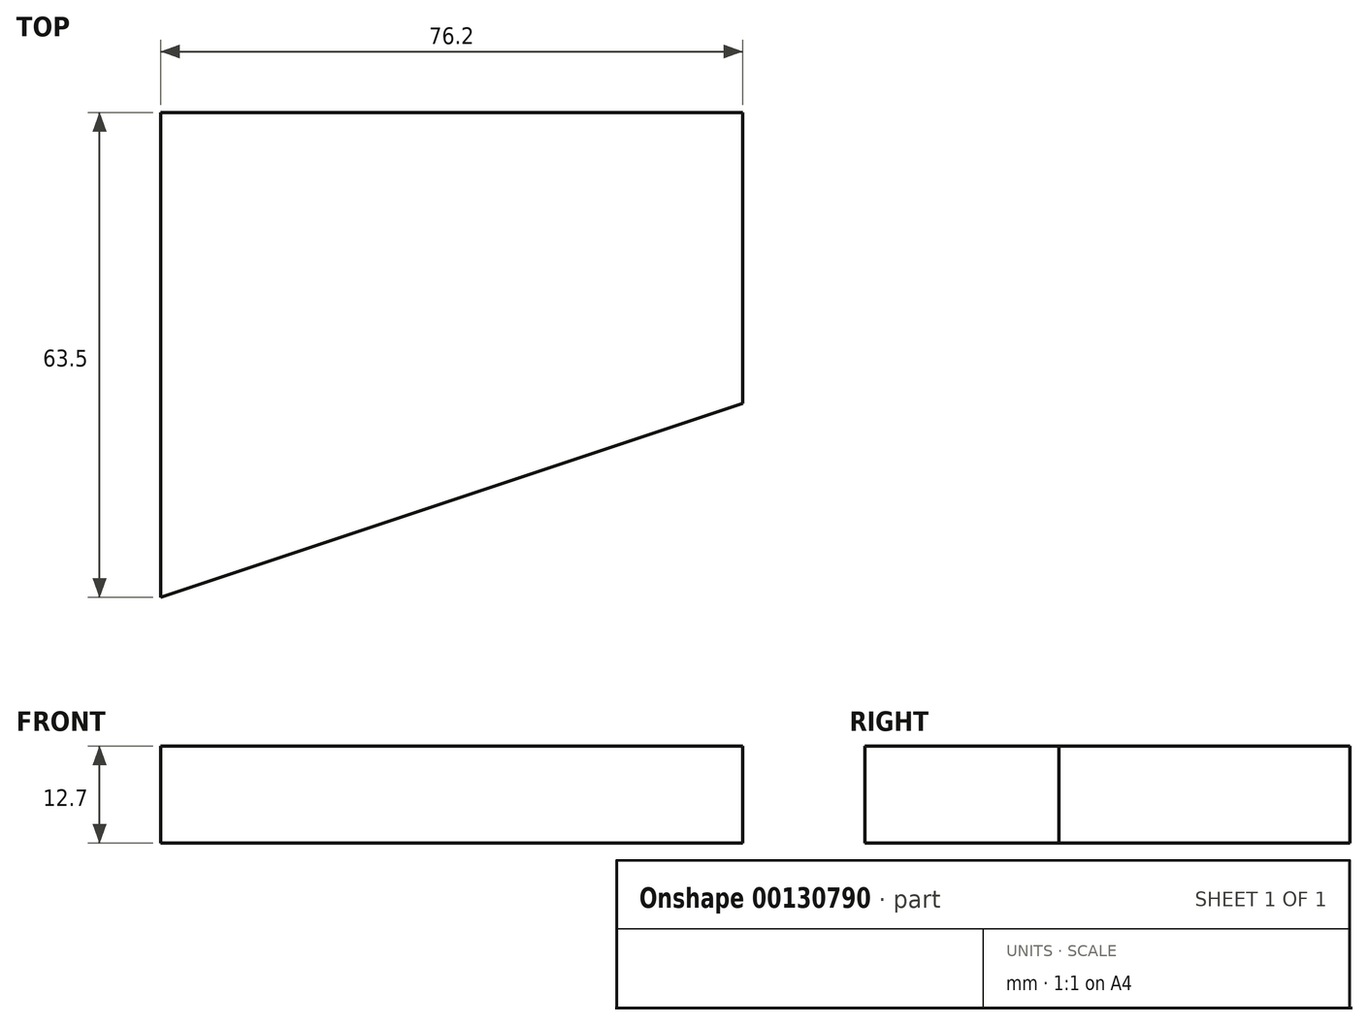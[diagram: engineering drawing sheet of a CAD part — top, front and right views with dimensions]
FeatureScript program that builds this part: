
annotation { "Feature Type Name" : "Feature", "Feature Type Description" : "" }
export const myFeature = defineFeature(function(context is Context, id is Id, definition is map)
    precondition{}
    {
        {
            var Q0;
            Q0=qCreatedBy(makeId("Front.planeOp"),FACE);
            var sketch = newSketch(context, id + "F0", { "sketchPlane" : qUnion([Q0])});
            skLineSegment(sketch, "E0.bottom", {"start": v(0, 0) * mm, "end": v(76.2, 0) * mm});
            skLineSegment(sketch, "E0.top", {"start": v(0, 50.8) * mm, "end": v(76.2, 50.8) * mm});
            skLineSegment(sketch, "E0.left", {"start": v(0, 0) * mm, "end": v(0, 50.8) * mm});
            skLineSegment(sketch, "E0.right", {"start": v(76.2, 0) * mm, "end": v(76.2, 50.8) * mm});
            skLineSegment(sketch, "E1.bottom", {"start": v(76.2, 50.8) * mm, "end": v(25.4, 50.8) * mm});
            skLineSegment(sketch, "E1.top", {"start": v(76.2, 12.7) * mm, "end": v(25.4, 12.7) * mm});
            skLineSegment(sketch, "E1.left", {"start": v(76.2, 50.8) * mm, "end": v(76.2, 12.7) * mm});
            skLineSegment(sketch, "E1.right", {"start": v(25.4, 50.8) * mm, "end": v(25.4, 12.7) * mm});
            skSolve(sketch);
        }
        {
            var Q0;
            Q0=makeQuery(id+"F0.imprint","IMPRINT",FACE,{"disambiguationData":[TD([[makeQuery(id+"F0.imprint","IMPRINT",EDGE,{"derivedFrom":sQuery(id+"F0.wireOp",EDGE,"E0.bottom")}),1.0]])]});
            var Q1;
            Q1=makeQuery(id+"F0.imprint","IMPRINT",FACE,{"disambiguationData":[TD([[makeQuery(id+"F0.imprint","IMPRINT",EDGE,{"derivedFrom":sQuery(id+"F0.wireOp",EDGE,"E1.bottom")}),1.0]])]});
            extrude(context, id + "F1", {"entities" : qUnion([Q0, Q1]), "oppositeDirection" : true, "depth" : 63.5 * mm});
        }
        {
            var Q0;
            Q0=makeQuery(id+"F1.opExtrude","SWEPT_FACE",FACE,{"disambiguationData":[OSD([sQuery(id+"F0.wireOp",EDGE,"E0.top"),sQuery(id+"F0.wireOp",EDGE,"E1.bottom")])]});
            var sketch = newSketch(context, id + "F2", { "sketchPlane" : qUnion([Q0])});
            skLineSegment(sketch, "E2", {"start": v(0, 0) * mm, "end": v(76.2, 25.4) * mm});
            skLineSegment(sketch, "E3", {"start": v(76.2, 25.4) * mm, "end": v(76.2, 0) * mm});
            skLineSegment(sketch, "E4", {"start": v(76.2, 0) * mm, "end": v(0, 0) * mm});
            skLineSegment(sketch, "E5", {"start": v(25.4, 8.47) * mm, "end": v(25.4, 50.8) * mm});
            skLineSegment(sketch, "E6", {"start": v(25.4, 50.8) * mm, "end": v(76.2, 50.8) * mm});
            skSolve(sketch);
        }
        {
            var Q0;
            Q0 = qSketchRegion(id + "F2", true);
            extrude(context, id + "F3", {"entities" : qUnion([Q0]), "operationType" : NewBodyOperationType.REMOVE, "oppositeDirection" : true, "depth" : 50.8 * mm});
        }
        {
            var Q0;
            {var subQ3=sQuery(id+"F2.wireOp",EDGE,"E5");Q0=makeQuery(id+"F2.imprint","IMPRINT",FACE,{"disambiguationData":[TD([[makeQuery(id+"F2.imprint","IMPRINT",EDGE,{"derivedFrom":subQ3}),-1.0]])]});}
            extrude(context, id + "F4", {"entities" : qUnion([Q0]), "operationType" : NewBodyOperationType.REMOVE, "oppositeDirection" : true, "depth" : 38.1 * mm});
        }
    });
